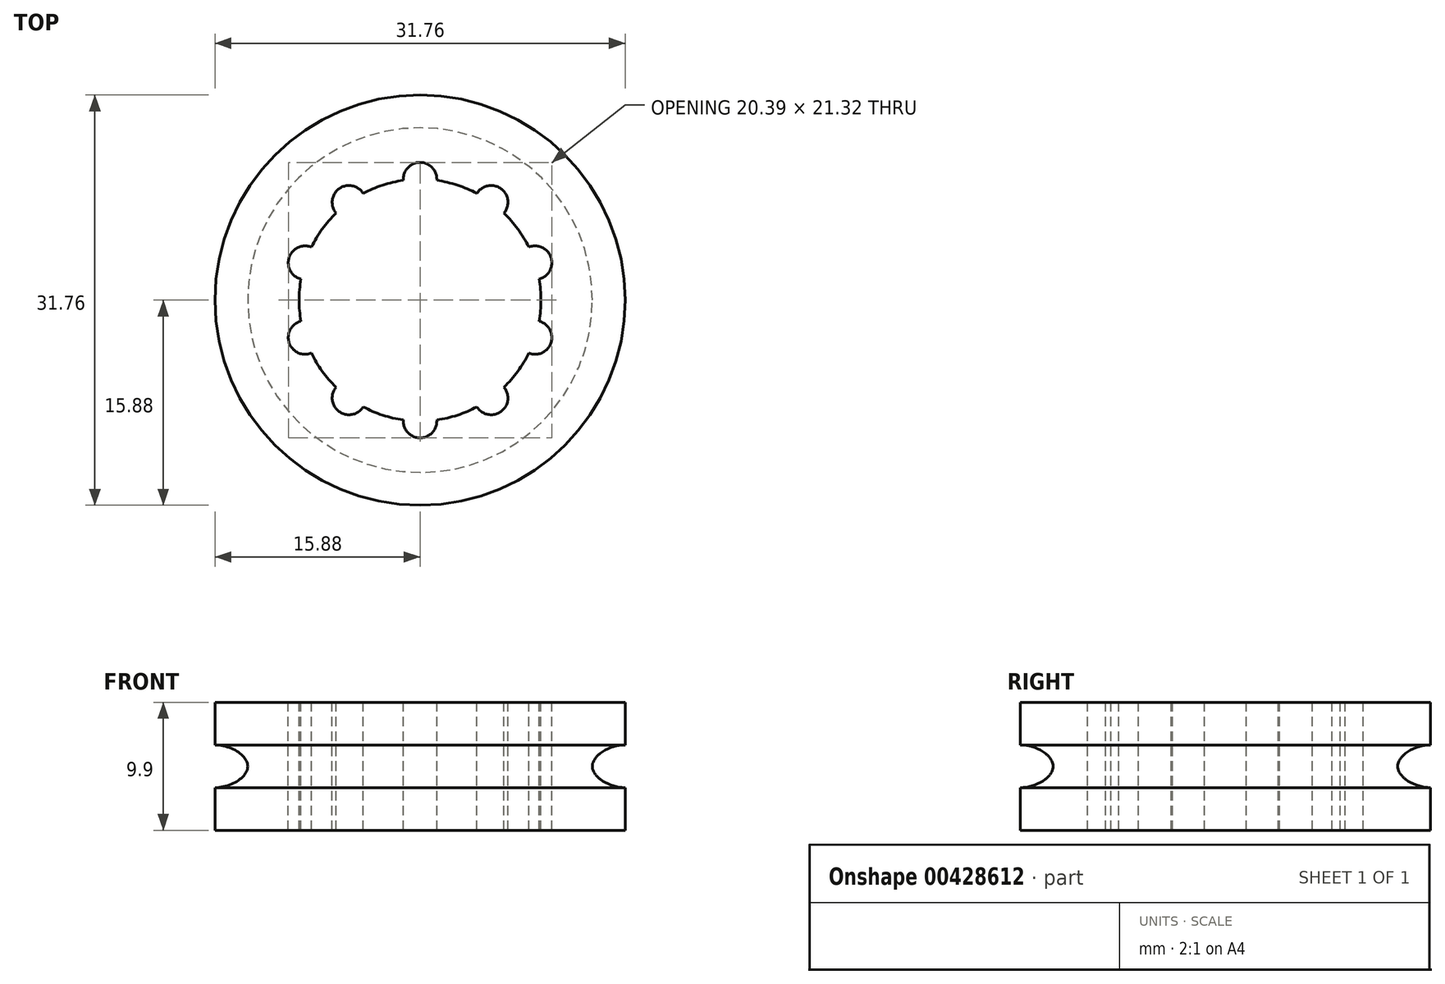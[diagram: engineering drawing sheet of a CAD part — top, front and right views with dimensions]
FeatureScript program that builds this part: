
annotation { "Feature Type Name" : "Feature", "Feature Type Description" : "" }
export const myFeature = defineFeature(function(context is Context, id is Id, definition is map)
    precondition{}
    {
        {
            var Q0;
            Q0=qCreatedBy(makeId("Front.planeOp"),FACE);
            var sketch = newSketch(context, id + "F0", { "sketchPlane" : qUnion([Q0])});
            skLineSegment(sketch, "E0", {"start": v(0, 4.95) * mm, "end": v(-15.88, 4.95) * mm});
            skLineSegment(sketch, "E1", {"start": v(-15.88, 4.95) * mm, "end": v(-15.88, 1.65) * mm});
            skLineSegment(sketch, "E2", {"start": v(-15.88, 1.65) * mm, "end": v(-13.33, 1.65) * mm});
            skLineSegment(sketch, "E3", {"start": v(-13.33, 1.65) * mm, "end": v(-13.33, 0) * mm});
            skLineSegment(sketch, "E4", {"start": v(0, 4.95) * mm, "end": v(0, 0) * mm});
            skLineSegment(sketch, "E5", {"start": v(0, 0) * mm, "end": v(-13.33, 0) * mm});
            skLineSegment(sketch, "E6", {"start": v(0, 0) * mm, "end": v(0, 23.56) * mm, "construction": true});
            skFitSpline(sketch, "E7", {"points": [v(-15.88, 1.65) * mm, v(-13.33, 0) * mm], "startDerivative": vector(3.81, 0) * mm, "endDerivative": vector(0, -2.48) * mm});
            skSolve(sketch);
        }
        {
            var Q0;
            Q0=qSketchRegion(id+"F0",true);
            var Q1;
            Q1=sQuery(id+"F0.wireOp",EDGE,"E6");
            revolve(context, id + "F1", {"entities" : qUnion([Q0]), "axis" : qUnion([Q1]), "revolveType" : RevolveType.FULL});
        }
        {
            var Q0;
            Q0=makeQuery(id+"F1.opRevolve","SWEPT_BODY",BODY,{"disambiguationData":[OSD([sQuery(id+"F0.wireOp",EDGE,"E0"),sQuery(id+"F0.wireOp",EDGE,"E1"),sQuery(id+"F0.wireOp",EDGE,"E2"),sQuery(id+"F0.wireOp",EDGE,"E3"),sQuery(id+"F0.wireOp",EDGE,"E4"),sQuery(id+"F0.wireOp",EDGE,"E5")])]});
            var Q1;
            Q1=qCreatedBy(makeId("Top.planeOp"),FACE);
            mirror(context, id + "F2", {"operationType" : NewBodyOperationType.ADD, "entities" : qUnion([Q0]), "mirrorPlane" : qUnion([Q1])});
        }
        {
            var Q0;
            Q0=makeQuery(id+"F1.opRevolve","SWEPT_FACE",FACE,{"disambiguationData":[OSD([sQuery(id+"F0.wireOp",EDGE,"E0")])]});
            var sketch = newSketch(context, id + "F3", { "sketchPlane" : qUnion([Q0])});
            skCircle(sketch, "E8", {"center": v(0, 0) * mm, "radius": 9.36 * mm});
            skCircle(sketch, "E9", {"center": v(0, 9.36) * mm, "radius": 1.3 * mm});
            skCircle(sketch, "E10.1.0", {"center": v(-5.5, 7.57) * mm, "radius": 1.3 * mm});
            skCircle(sketch, "E10.2.0", {"center": v(-8.9, 2.9) * mm, "radius": 1.3 * mm});
            skCircle(sketch, "E10.3.0", {"center": v(-8.9, -2.9) * mm, "radius": 1.3 * mm});
            skCircle(sketch, "E10.4.0", {"center": v(-5.5, -7.57) * mm, "radius": 1.3 * mm});
            skCircle(sketch, "E10.5.0", {"center": v(0, -9.36) * mm, "radius": 1.3 * mm});
            skCircle(sketch, "E10.6.0", {"center": v(5.5, -7.57) * mm, "radius": 1.3 * mm});
            skCircle(sketch, "E10.7.0", {"center": v(8.9, -2.9) * mm, "radius": 1.3 * mm});
            skCircle(sketch, "E10.8.0", {"center": v(8.9, 2.9) * mm, "radius": 1.3 * mm});
            skCircle(sketch, "E10.9.0", {"center": v(5.5, 7.57) * mm, "radius": 1.3 * mm});
            skSolve(sketch);
        }
        {
            var Q0;
            Q0=qSketchRegion(id+"F3",true);
            extrude(context, id + "F4", {"entities" : qUnion([Q0]), "operationType" : NewBodyOperationType.REMOVE, "endBound" : BoundingType.THROUGH_ALL, "oppositeDirection" : true, "depth" : 25.4 * mm});
        }
    });
